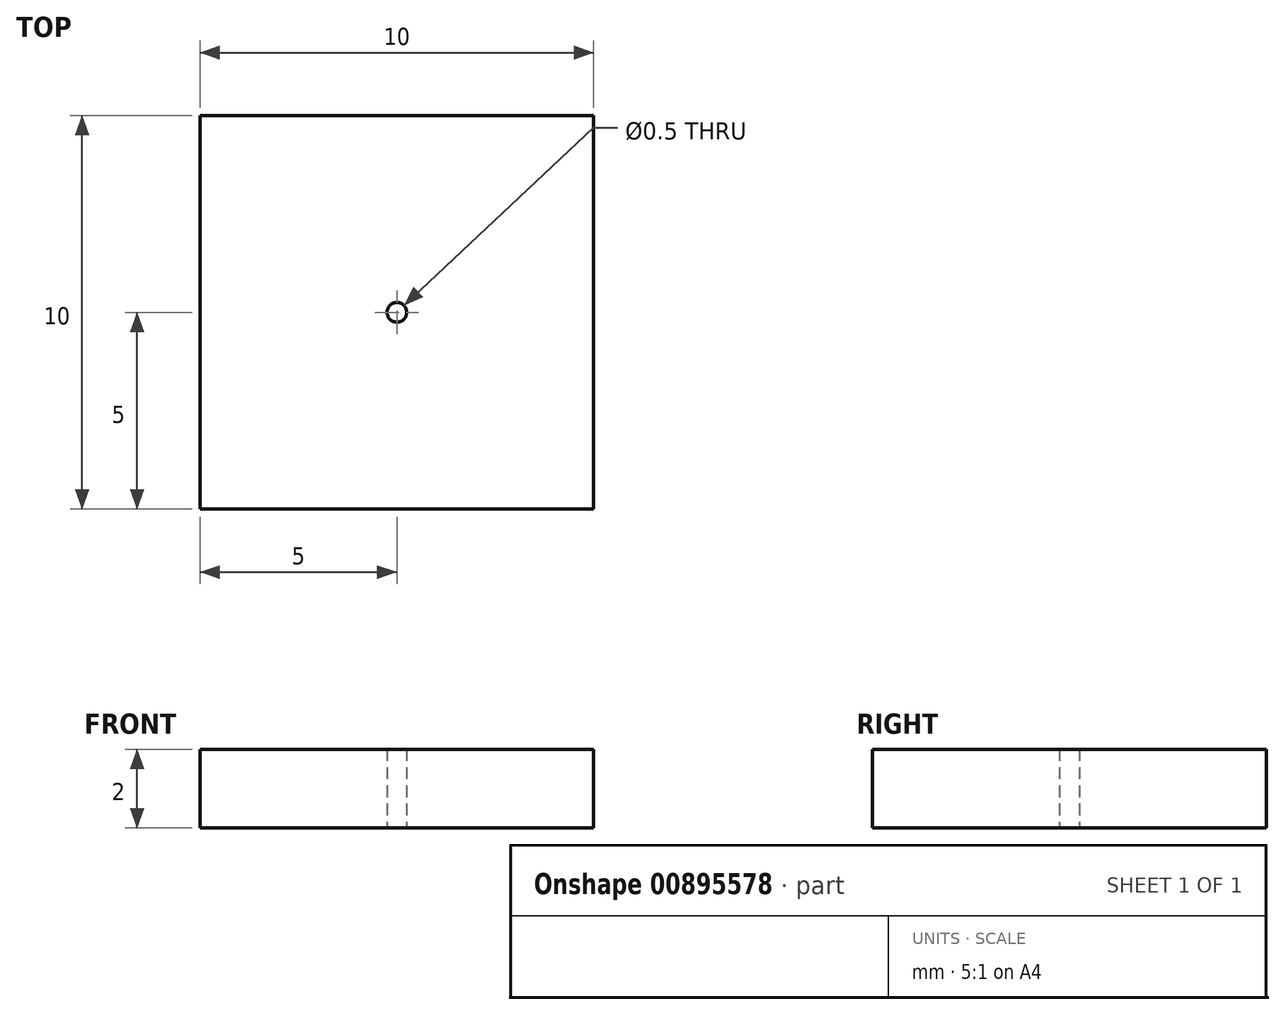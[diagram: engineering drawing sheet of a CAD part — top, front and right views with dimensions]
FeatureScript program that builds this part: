
annotation { "Feature Type Name" : "Feature", "Feature Type Description" : "" }
export const myFeature = defineFeature(function(context is Context, id is Id, definition is map)
    precondition{}
    {
        {
            var Q0;
            Q0=qCreatedBy(makeId("Top.planeOp"),FACE);
            var sketch = newSketch(context, id + "F0", { "sketchPlane" : qUnion([Q0])});
            skLineSegment(sketch, "E0.bottom", {"start": v(-5, 5) * mm, "end": v(5, 5) * mm});
            skLineSegment(sketch, "E0.top", {"start": v(-5, -5) * mm, "end": v(5, -5) * mm});
            skLineSegment(sketch, "E0.left", {"start": v(-5, 5) * mm, "end": v(-5, -5) * mm});
            skLineSegment(sketch, "E0.right", {"start": v(5, 5) * mm, "end": v(5, -5) * mm});
            skCircle(sketch, "E1", {"center": v(0, 0) * mm, "radius": 0.25 * mm});
            skSolve(sketch);
        }
        {
            var Q0;
            Q0=makeQuery(id+"F0.imprint","IMPRINT",FACE,{"disambiguationData":[TD([[makeQuery(id+"F0.imprint","IMPRINT",EDGE,{"derivedFrom":sQuery(id+"F0.wireOp",EDGE,"E0.bottom")}),-1.0]])]});
            extrude(context, id + "F1", {"entities" : qUnion([Q0]), "depth" : 2 * mm, "offsetDistance" : 25 * mm});
        }
    });
